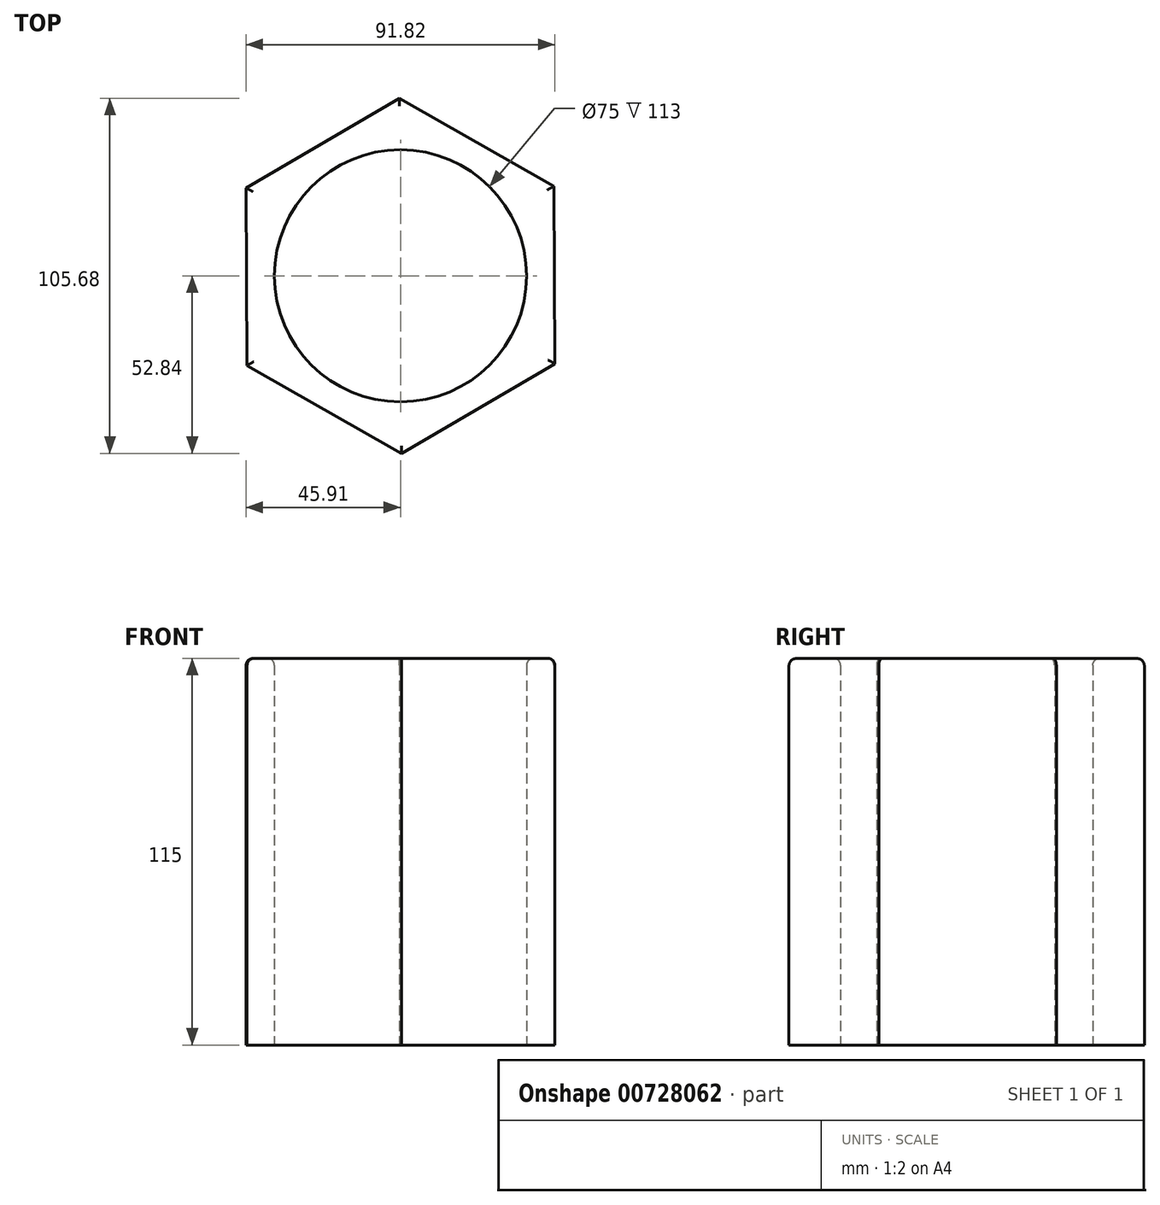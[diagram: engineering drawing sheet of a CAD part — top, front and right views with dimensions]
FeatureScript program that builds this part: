
annotation { "Feature Type Name" : "Feature", "Feature Type Description" : "" }
export const myFeature = defineFeature(function(context is Context, id is Id, definition is map)
    precondition{}
    {
        {
            var Q0;
            Q0=qCreatedBy(makeId("Top.planeOp"),FACE);
            var sketch = newSketch(context, id + "F0", { "sketchPlane" : qUnion([Q0])});
            skCircle(sketch, "E0.cCircle", {"center": v(0, 0) * mm, "radius": 52.84 * mm, "construction": true});
            skLineSegment(sketch, "E0.0", {"start": v(45.61, 26.68) * mm, "end": v(45.9, -26.16) * mm});
            skLineSegment(sketch, "E0.1", {"start": v(45.9, -26.16) * mm, "end": v(0.3, -52.84) * mm});
            skLineSegment(sketch, "E0.2", {"start": v(0.3, -52.84) * mm, "end": v(-45.61, -26.68) * mm});
            skLineSegment(sketch, "E0.3", {"start": v(-45.61, -26.68) * mm, "end": v(-45.9, 26.16) * mm});
            skLineSegment(sketch, "E0.4", {"start": v(-45.9, 26.16) * mm, "end": v(-0.3, 52.84) * mm});
            skLineSegment(sketch, "E0.5", {"start": v(-0.3, 52.84) * mm, "end": v(45.61, 26.68) * mm});
            skCircle(sketch, "E1", {"center": v(0, 0) * mm, "radius": 37.5 * mm});
            skSolve(sketch);
        }
        {
            var Q0;
            Q0=makeQuery(id+"F0.imprint","IMPRINT",FACE,{"disambiguationData":[TD([[makeQuery(id+"F0.imprint","IMPRINT",EDGE,{"derivedFrom":sQuery(id+"F0.wireOp",EDGE,"E0.0")}),-1.0]])]});
            extrude(context, id + "F1", {"entities" : qUnion([Q0]), "depth" : 115 * mm, "offsetDistance" : 25 * mm});
        }
        {
            var Q0;
            Q0=makeQuery(id+"F1.opExtrude","CAP_EDGE",EDGE,{"disambiguationData":[OSD([sQuery(id+"F0.wireOp",EDGE,"E0.1")])],"isStart":false});
            var Q1;
            Q1=makeQuery(id+"F1.opExtrude","CAP_EDGE",EDGE,{"disambiguationData":[OSD([sQuery(id+"F0.wireOp",EDGE,"E0.2")])],"isStart":false});
            var Q2;
            Q2=makeQuery(id+"F1.opExtrude","CAP_EDGE",EDGE,{"disambiguationData":[OSD([sQuery(id+"F0.wireOp",EDGE,"E0.3")])],"isStart":false});
            var Q3;
            Q3=makeQuery(id+"F1.opExtrude","CAP_EDGE",EDGE,{"disambiguationData":[OSD([sQuery(id+"F0.wireOp",EDGE,"E0.4")])],"isStart":false});
            var Q4;
            Q4=makeQuery(id+"F1.opExtrude","CAP_EDGE",EDGE,{"disambiguationData":[OSD([sQuery(id+"F0.wireOp",EDGE,"E0.5")])],"isStart":false});
            var Q5;
            Q5=makeQuery(id+"F1.opExtrude","CAP_EDGE",EDGE,{"disambiguationData":[OSD([sQuery(id+"F0.wireOp",EDGE,"E0.0")])],"isStart":false});
            var Q6;
            Q6=makeQuery(id+"F1.opExtrude","CAP_EDGE",EDGE,{"disambiguationData":[OSD([sQuery(id+"F0.wireOp",EDGE,"E1")])],"isStart":false});
            fillet(context, id + "F2", {"entities" : qUnion([Q0, Q1, Q2, Q3, Q4, Q5, Q6]), "radius" : 2 * mm, "tangentPropagation" : true, "allowEdgeOverflow" : false});
        }
    });
